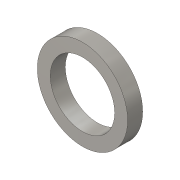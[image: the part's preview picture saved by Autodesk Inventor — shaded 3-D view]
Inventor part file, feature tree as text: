
AUTODESK INVENTOR PART (.ipt)
format: ipt  version: 2016 (Build 200138000, 138)  size: 81,408 bytes
history: native  units: in
note: dims shown in document units (in); Inventor stores cm internally (conversion verified against a paired STEP export)
features: extrude x1, sketch x1
ambient origin geometry x8: Origin, YZ Plane, XZ Plane, XY Plane, X Axis, Y Axis, Z Axis, Center Point
bodies: Solid1 (feature_tree)
feature tree (2):
  extrude  "Extrusion1"  Depth=0.2756in
  sketch  "Sketch2"  dims[d0=1.1811in d1=1.6535in d2=0.2756in d3=0.0in]
